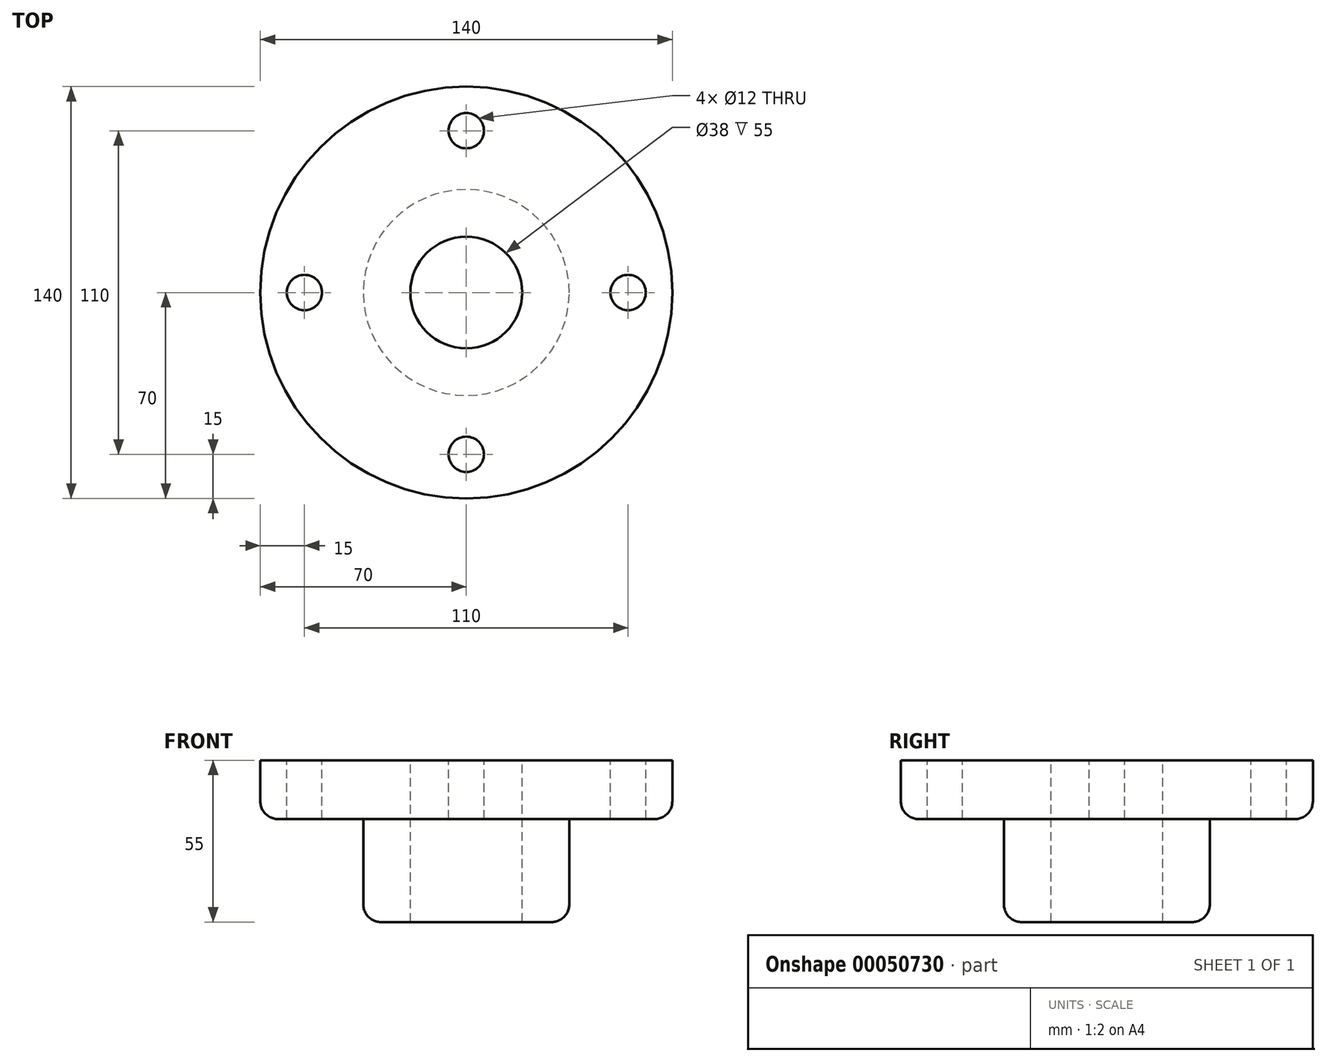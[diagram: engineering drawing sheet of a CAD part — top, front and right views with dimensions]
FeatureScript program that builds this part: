
annotation { "Feature Type Name" : "Feature", "Feature Type Description" : "" }
export const myFeature = defineFeature(function(context is Context, id is Id, definition is map)
    precondition{}
    {
        {
            var Q0;
            Q0=qCreatedBy(makeId("Top.planeOp"),FACE);
            var sketch = newSketch(context, id + "F0", { "sketchPlane" : qUnion([Q0])});
            skCircle(sketch, "E0", {"center": v(0, 0) * mm, "radius": 70 * mm});
            skCircle(sketch, "E1", {"center": v(0, 0) * mm, "radius": 35 * mm});
            skCircle(sketch, "E2", {"center": v(0, 0) * mm, "radius": 19 * mm});
            skCircle(sketch, "E3", {"center": v(0, 0) * mm, "radius": 55 * mm, "construction": true});
            skCircle(sketch, "E4", {"center": v(0, 55) * mm, "radius": 6 * mm});
            skCircle(sketch, "E5.1.0", {"center": v(-55, 0) * mm, "radius": 6 * mm});
            skCircle(sketch, "E5.2.0", {"center": v(0, -55) * mm, "radius": 6 * mm});
            skCircle(sketch, "E5.3.0", {"center": v(55, 0) * mm, "radius": 6 * mm});
            skSolve(sketch);
        }
        {
            var Q0;
            Q0=makeQuery(id+"F0.imprint","IMPRINT",FACE,{"disambiguationData":[TD([[makeQuery(id+"F0.imprint","IMPRINT",EDGE,{"derivedFrom":sQuery(id+"F0.wireOp",EDGE,"E0")}),1.0]])]});
            extrude(context, id + "F1", {"entities" : qUnion([Q0]), "oppositeDirection" : true, "depth" : 20 * mm});
        }
        {
            var Q0;
            Q0=makeQuery(id+"F0.imprint","IMPRINT",FACE,{"disambiguationData":[TD([[makeQuery(id+"F0.imprint","IMPRINT",EDGE,{"derivedFrom":sQuery(id+"F0.wireOp",EDGE,"E1")}),1.0]])]});
            extrude(context, id + "F2", {"entities" : qUnion([Q0]), "operationType" : NewBodyOperationType.ADD, "oppositeDirection" : true, "depth" : 55 * mm});
        }
        {
            var Q0;
            Q0=makeQuery(id+"F1.opExtrude","CAP_EDGE",EDGE,{"disambiguationData":[OSD([sQuery(id+"F0.wireOp",EDGE,"E0")])],"isStart":false});
            var Q1;
            Q1=makeQuery(id+"F2.opExtrude","CAP_EDGE",EDGE,{"disambiguationData":[OSD([sQuery(id+"F0.wireOp",EDGE,"E1")])],"isStart":false});
            var Q2;
            Q2=makeQuery(id+"F1.opExtrude","CAP_EDGE",EDGE,{"disambiguationData":[OSD([sQuery(id+"F0.wireOp",EDGE,"E1")])],"isStart":false});
            fillet(context, id + "F3", {"entities" : qUnion([Q0, Q1, Q2]), "radius" : 6 * mm, "tangentPropagation" : true, "allowEdgeOverflow" : false});
        }
    });
